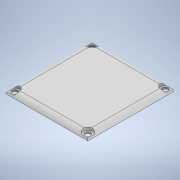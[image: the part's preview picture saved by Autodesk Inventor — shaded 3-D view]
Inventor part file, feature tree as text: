
AUTODESK INVENTOR PART (.ipt)
format: ipt  version: 2020 (Build 240168000, 168)  size: 148,480 bytes
history: native  units: in
note: dims shown in document units (in); Inventor stores cm internally (conversion verified against a paired STEP export)
features: sketch x2, extrude x1, hole x1, fillet x1
ambient origin geometry x8: Origin, YZ Plane, XZ Plane, XY Plane, X Axis, Y Axis, Z Axis, Center Point
bodies: Solid1 (feature_tree)
feature tree (5):
  extrude  "Extrusion1"  Depth=1.975in
  hole  "Hole1"  [1 undecoded]
  fillet  "Fillet1"  Radius=0.1in
  sketch  "Sketch1"  dims[d0=1.875in d1=1.975in]
  sketch  "Sketch2"  dims[d2=0.1in d3=0.0in d4=0.1in d5=0.1in d6=0.1in d7=0.1in d8=0.129in d9=0.75in d10=0.219in d11=0.0625in d12=0.5635in d13=0.224in d14=0.0in d15=0.125in]
note: 1 required parameter value undecoded (feature->parameter linkage not recoverable at this tier; creation-order binding heuristic only, values carry confidence <= 0.55)
